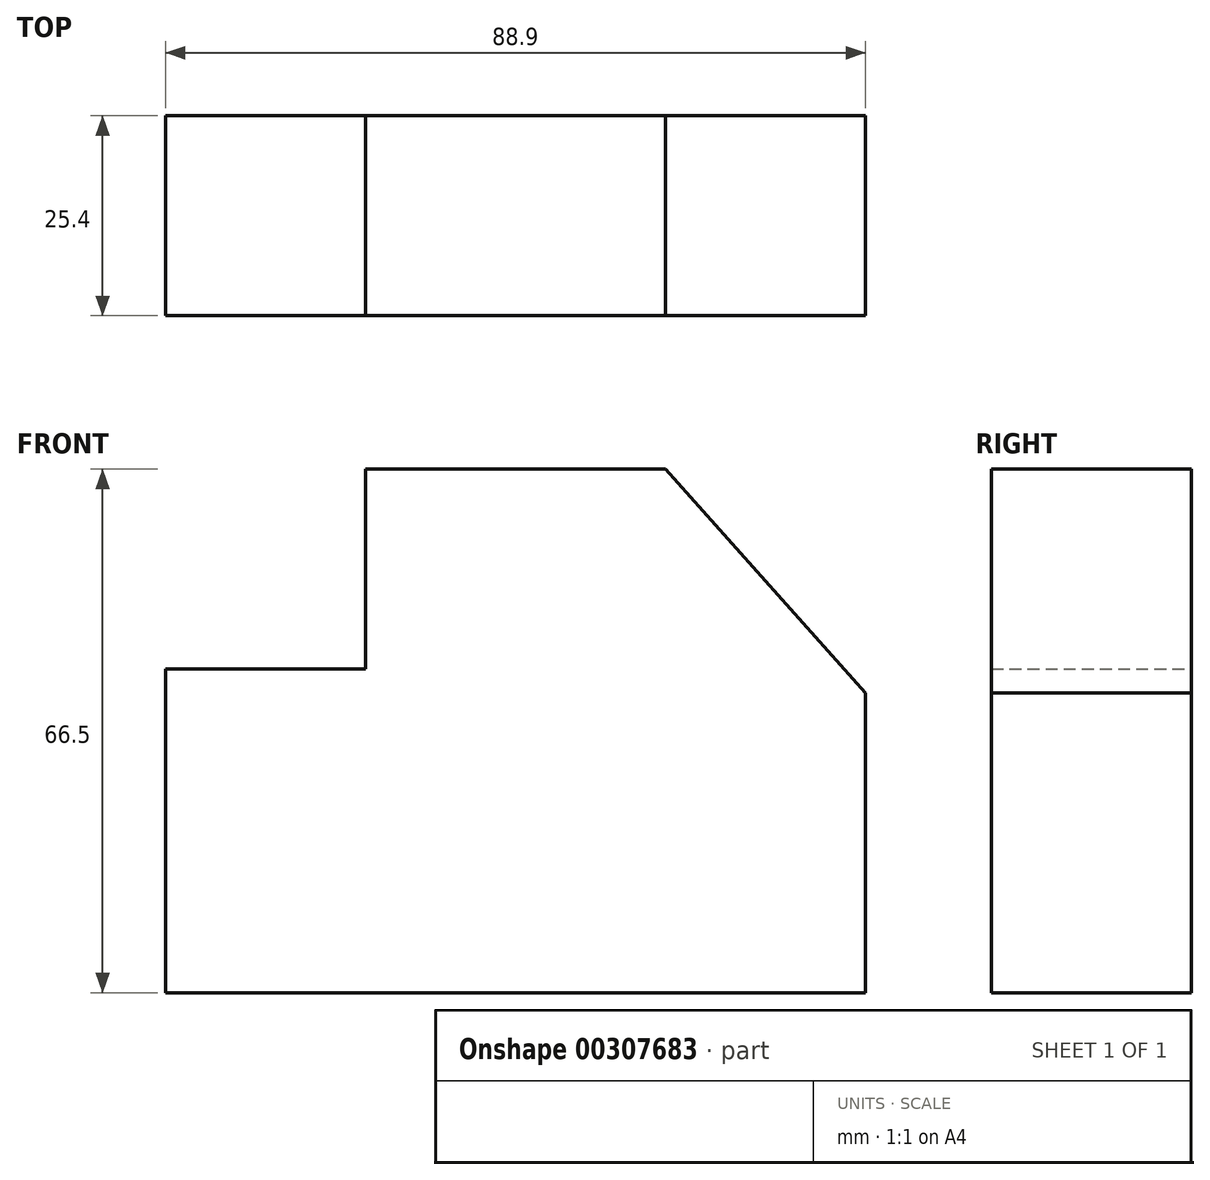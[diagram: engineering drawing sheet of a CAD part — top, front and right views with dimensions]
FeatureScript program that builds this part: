
annotation { "Feature Type Name" : "Feature", "Feature Type Description" : "" }
export const myFeature = defineFeature(function(context is Context, id is Id, definition is map)
    precondition{}
    {
        {
            var Q0;
            Q0=qCreatedBy(makeId("Front.planeOp"),FACE);
            var sketch = newSketch(context, id + "F0", { "sketchPlane" : qUnion([Q0])});
            skLineSegment(sketch, "E0", {"start": v(-60.1, -42.45) * mm, "end": v(28.8, -42.45) * mm});
            skLineSegment(sketch, "E1", {"start": v(28.8, -42.45) * mm, "end": v(28.8, -4.35) * mm});
            skLineSegment(sketch, "E2", {"start": v(28.8, -4.35) * mm, "end": v(3.4, 24.05) * mm});
            skLineSegment(sketch, "E3", {"start": v(3.4, 24.05) * mm, "end": v(-34.7, 24.05) * mm});
            skLineSegment(sketch, "E4", {"start": v(-34.7, 24.05) * mm, "end": v(-34.7, -1.35) * mm});
            skLineSegment(sketch, "E5", {"start": v(-34.7, -1.35) * mm, "end": v(-60.1, -1.35) * mm});
            skLineSegment(sketch, "E6", {"start": v(-60.1, -1.35) * mm, "end": v(-60.1, -42.45) * mm});
            skSolve(sketch);
        }
        {
            var Q0;
            Q0=makeQuery(id+"F0.imprint","IMPRINT",FACE,{"disambiguationData":[TD([[makeQuery(id+"F0.imprint","IMPRINT",EDGE,{"derivedFrom":sQuery(id+"F0.wireOp",EDGE,"E0")}),1.0]])]});
            extrude(context, id + "F1", {"entities" : qUnion([Q0]), "depth" : 25.4 * mm});
        }
    });
